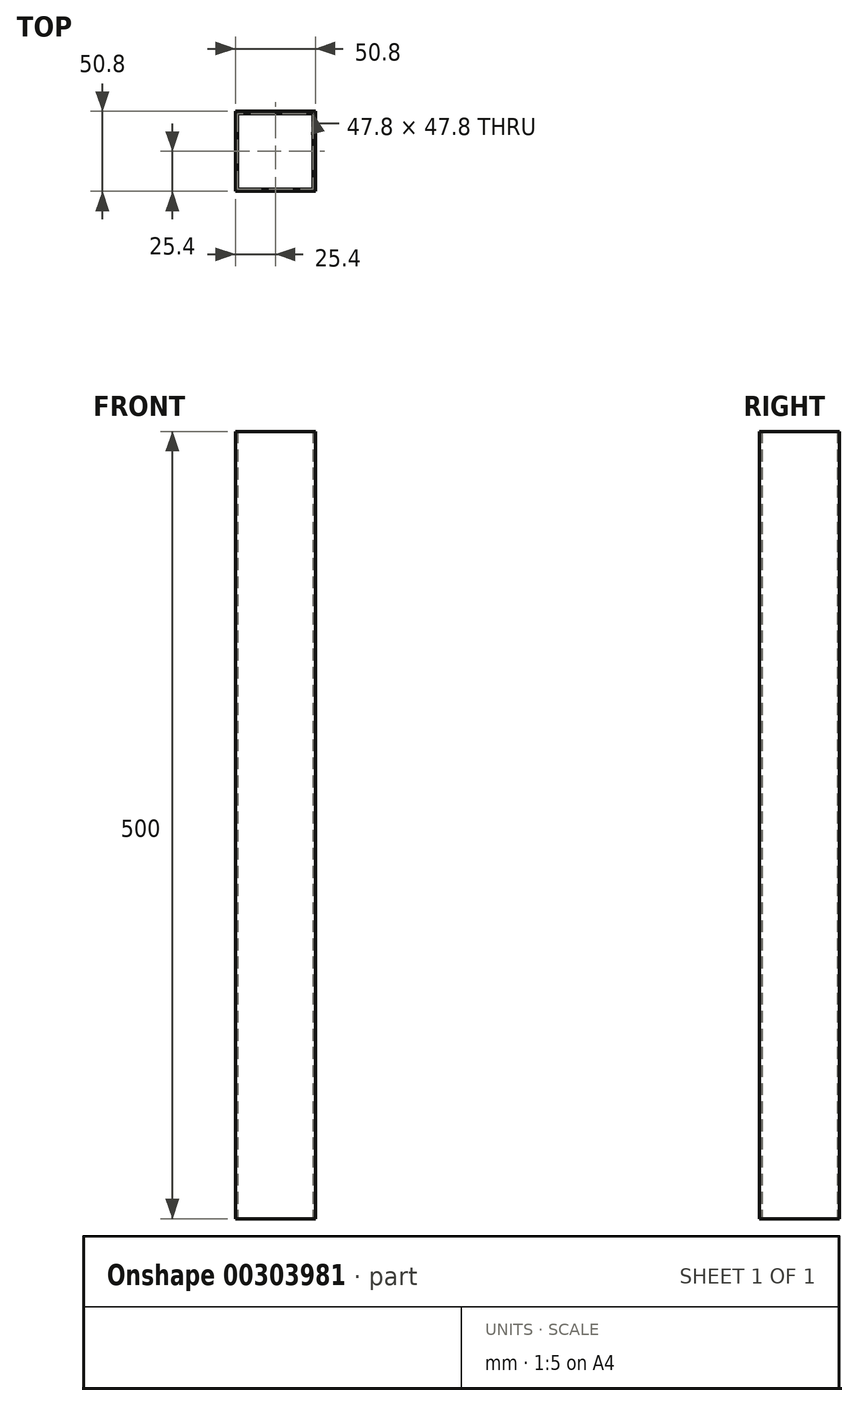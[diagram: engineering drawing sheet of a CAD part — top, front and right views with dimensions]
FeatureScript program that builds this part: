
annotation { "Feature Type Name" : "Feature", "Feature Type Description" : "" }
export const myFeature = defineFeature(function(context is Context, id is Id, definition is map)
    precondition{}
    {
        {
            var Q0;
            Q0=qCreatedBy(makeId("Top.planeOp"),FACE);
            var sketch = newSketch(context, id + "F0", { "sketchPlane" : qUnion([Q0])});
            skLineSegment(sketch, "E0.bottom", {"start": v(0, 0) * mm, "end": v(50.8, 0) * mm});
            skLineSegment(sketch, "E0.top", {"start": v(0, 50.8) * mm, "end": v(50.8, 50.8) * mm});
            skLineSegment(sketch, "E0.left", {"start": v(0, 0) * mm, "end": v(0, 50.8) * mm});
            skLineSegment(sketch, "E0.right", {"start": v(50.8, 0) * mm, "end": v(50.8, 50.8) * mm});
            skLineSegment(sketch, "E1.0", {"start": v(1.5, 49.3) * mm, "end": v(49.3, 49.3) * mm});
            skLineSegment(sketch, "E1.1", {"start": v(1.5, 1.5) * mm, "end": v(1.5, 49.3) * mm});
            skLineSegment(sketch, "E1.2", {"start": v(1.5, 1.5) * mm, "end": v(49.3, 1.5) * mm});
            skLineSegment(sketch, "E1.3", {"start": v(49.3, 1.5) * mm, "end": v(49.3, 49.3) * mm});
            skSolve(sketch);
        }
        {
            var Q0;
            Q0=makeQuery(id+"F0.imprint","IMPRINT",FACE,{"disambiguationData":[TD([[makeQuery(id+"F0.imprint","IMPRINT",EDGE,{"derivedFrom":sQuery(id+"F0.wireOp",EDGE,"E0.bottom")}),1.0]])]});
            extrude(context, id + "F1", {"entities" : qUnion([Q0]), "depth" : 500 * mm});
        }
    });
